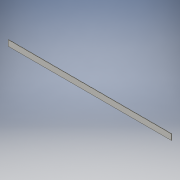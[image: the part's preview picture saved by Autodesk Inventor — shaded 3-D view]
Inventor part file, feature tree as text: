
AUTODESK INVENTOR PART (.ipt)
format: ipt  version: 2018 (Build 220112000, 112)  size: 93,696 bytes
history: native  units: mm
features: extrude x1, sketch x1
ambient origin geometry x8: Origin, YZ Plane, XZ Plane, XY Plane, X Axis, Y Axis, Z Axis, Center Point
bodies: Solid1 (feature_tree)
feature tree (2):
  extrude  "Extrusion1"  Depth=40.0mm
  sketch  "Sketch1"  dims[d0=1153.6mm d1=40.0mm d2=2.5mm d3=0.0mm]
